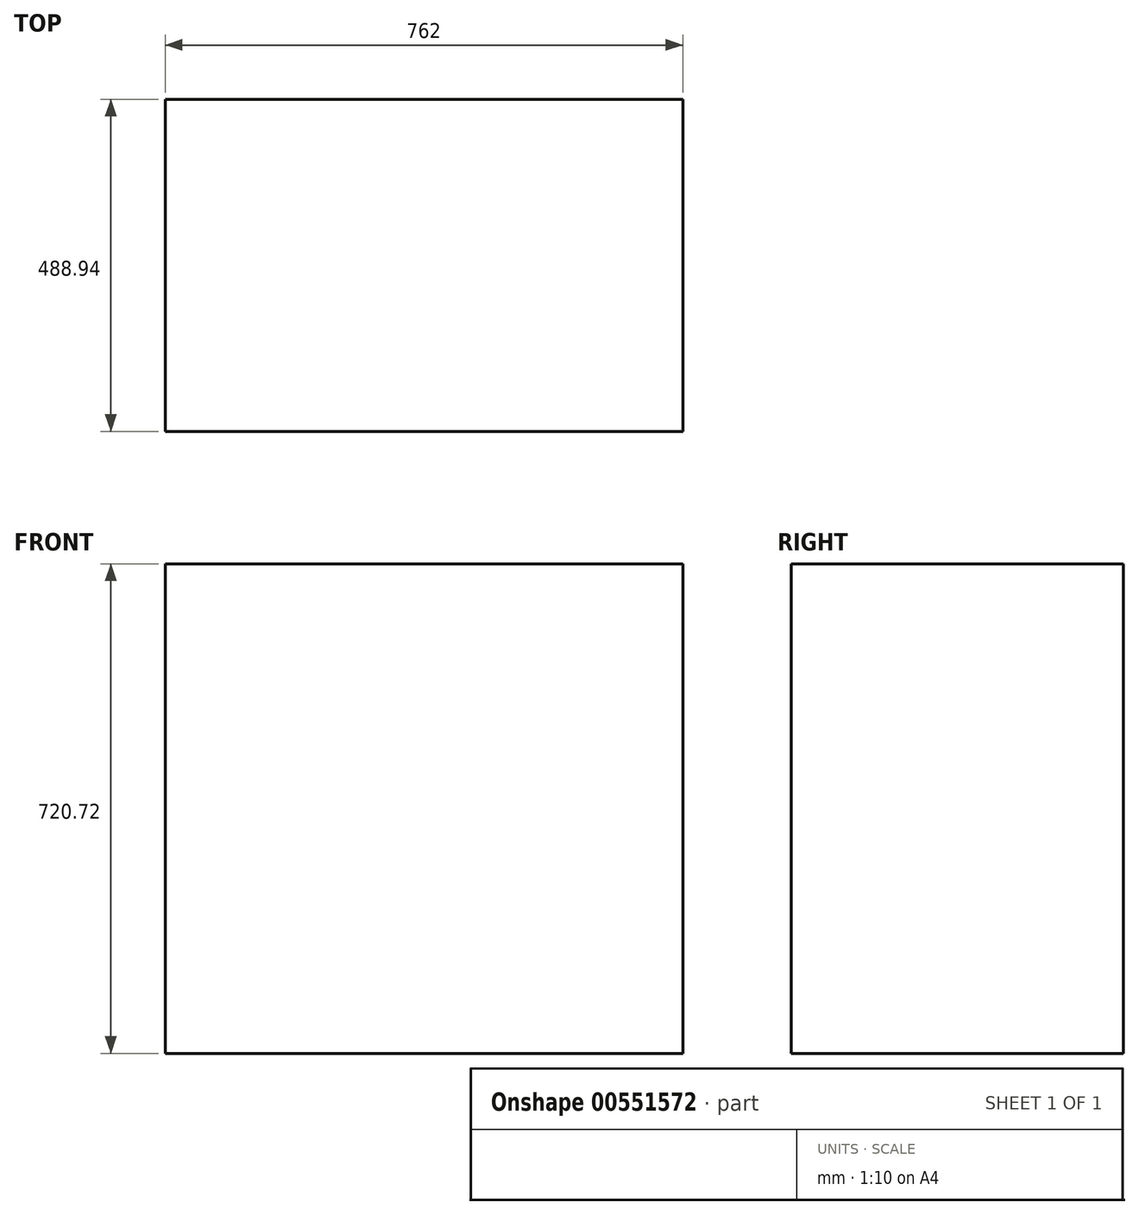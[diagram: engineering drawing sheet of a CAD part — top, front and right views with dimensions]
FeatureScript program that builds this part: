
annotation { "Feature Type Name" : "Feature", "Feature Type Description" : "" }
export const myFeature = defineFeature(function(context is Context, id is Id, definition is map)
    precondition{}
    {
        {
            var Q0;
            Q0=qCreatedBy(makeId("Top.planeOp"),FACE);
            var sketch = newSketch(context, id + "F0", { "sketchPlane" : qUnion([Q0])});
            skLineSegment(sketch, "E0.bottom", {"start": v(381, 244.47) * mm, "end": v(-381, 244.47) * mm});
            skLineSegment(sketch, "E0.top", {"start": v(381, -244.48) * mm, "end": v(-381, -244.48) * mm});
            skLineSegment(sketch, "E0.left", {"start": v(381, 244.47) * mm, "end": v(381, -244.48) * mm});
            skLineSegment(sketch, "E0.right", {"start": v(-381, 244.48) * mm, "end": v(-381, -244.48) * mm});
            skPoint(sketch, "E0.middle", {"position": v(0, 0) * mm});
            skSolve(sketch);
        }
        {
            var Q0;
            Q0=makeQuery(id+"F0.imprint","IMPRINT",FACE,{"disambiguationData":[TD([[makeQuery(id+"F0.imprint","IMPRINT",EDGE,{"derivedFrom":sQuery(id+"F0.wireOp",EDGE,"E0.bottom")}),1.0]])]});
            extrude(context, id + "F1", {"entities" : qUnion([Q0]), "depth" : 720.72 * mm, "offsetDistance" : 25.4 * mm});
        }
    });
